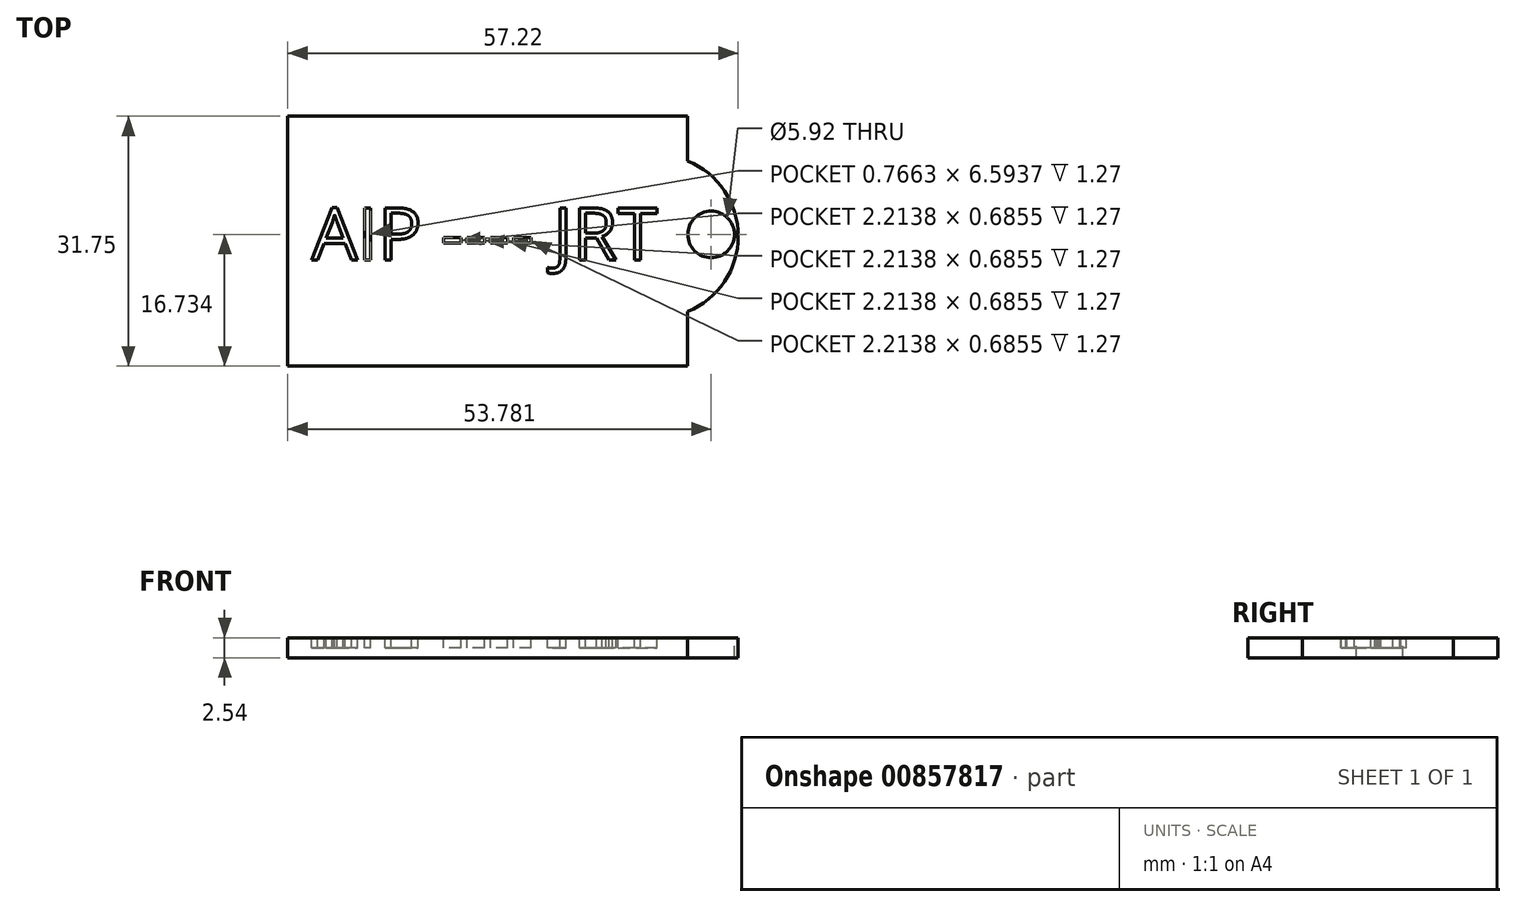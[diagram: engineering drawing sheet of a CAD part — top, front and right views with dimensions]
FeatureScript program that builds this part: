
annotation { "Feature Type Name" : "Feature", "Feature Type Description" : "" }
export const myFeature = defineFeature(function(context is Context, id is Id, definition is map)
    precondition{}
    {
        {
            var Q0;
            Q0=qCreatedBy(makeId("Top.planeOp"),FACE);
            var sketch = newSketch(context, id + "F0", { "sketchPlane" : qUnion([Q0])});
            skLineSegment(sketch, "E0.bottom", {"start": v(0, 0) * mm, "end": v(50.8, 0) * mm});
            skLineSegment(sketch, "E0.top", {"start": v(0, 31.75) * mm, "end": v(50.8, 31.75) * mm});
            skLineSegment(sketch, "E0.left", {"start": v(0, 0) * mm, "end": v(0, 31.75) * mm});
            skLineSegment(sketch, "E0.right", {"start": v(50.8, 0) * mm, "end": v(50.8, 31.75) * mm});
            skSolve(sketch);
        }
        {
            var Q0;
            Q0 = qSketchRegion(id + "F0", true);
            extrude(context, id + "F1", {"entities" : qUnion([Q0]), "depth" : 2.54 * mm, "offsetDistance" : 25.4 * mm});
        }
        {
            var Q0;
            Q0=makeQuery(id+"F1.opExtrude","CAP_FACE",FACE,{"disambiguationData":[OSD([sQuery(id+"F0.wireOp",EDGE,"E0.bottom"),sQuery(id+"F0.wireOp",EDGE,"E0.top"),sQuery(id+"F0.wireOp",EDGE,"E0.left"),sQuery(id+"F0.wireOp",EDGE,"E0.right")])],"isStart":false});
            var sketch = newSketch(context, id + "F2", { "sketchPlane" : qUnion([Q0])});
            skText(sketch, "E1", { "text": "AIP ---- JRT", "fontName": "OpenSans-Regular.ttf"});
            const initialGuessF2  = {"E1": [0.00303, 0.0135, 1, 0, 0.00665]};
            skSetInitialGuess(sketch, initialGuessF2);
            skSolve(sketch);
        }
        {
            var Q0;
            Q0 = qSketchRegion(id + "F2", true);
            extrude(context, id + "F3", {"entities" : qUnion([Q0]), "operationType" : NewBodyOperationType.REMOVE, "oppositeDirection" : true, "depth" : 1.27 * mm, "offsetDistance" : 25.4 * mm});
        }
        {
            var Q0;
            {var subQ0=sQuery(id+"F0.wireOp",EDGE,"E0.left");var subQ1=sQuery(id+"F0.wireOp",EDGE,"E0.bottom");var subQ2=sQuery(id+"F0.wireOp",EDGE,"E0.right");var subQ3=sQuery(id+"F0.wireOp",EDGE,"E0.top");Q0=makeQuery(id+"F3.boolean.opBoolean","SPLIT",FACE,{"disambiguationData":[TD([makeQuery(id+"F1.opExtrude","SWEPT_FACE",FACE,{"disambiguationData":[OSD([subQ1])]})])],"derivedFrom":makeQuery(id+"F1.opExtrude","CAP_FACE",FACE,{"disambiguationData":[OSD([subQ1,subQ3,subQ0,subQ2])],"isStart":false})});}
            var sketch = newSketch(context, id + "F4", { "sketchPlane" : qUnion([Q0])});
            skArc(sketch, "E2", {"start": v(50.8, 6.93) * mm, "mid": v(57.22, 16.5) * mm, "end": v(50.8, 26.07) * mm});
            skSolve(sketch);
        }
        {
            var Q0;
            {var subQ0=sQuery(id+"F4.wireOp",EDGE,"E2");Q0=makeQuery(id+"F4.imprint","IMPRINT",FACE,{"disambiguationData":[TD([[makeQuery(id+"F4.imprint","IMPRINT",EDGE,{"derivedFrom":subQ0}),1.0]])]});}
            var sketch = newSketch(context, id + "F5", { "sketchPlane" : qUnion([Q0])});
            skCircle(sketch, "E3", {"center": v(53.78, 16.73) * mm, "radius": 2.96 * mm});
            skSolve(sketch);
        }
        {
            var Q0;
            {var subQ0=sQuery(id+"F4.wireOp",EDGE,"E2");Q0=makeQuery(id+"F4.imprint","IMPRINT",FACE,{"disambiguationData":[TD([[makeQuery(id+"F4.imprint","IMPRINT",EDGE,{"derivedFrom":subQ0}),1.0]])]});}
            extrude(context, id + "F6", {"entities" : qUnion([Q0]), "operationType" : NewBodyOperationType.ADD, "oppositeDirection" : true, "depth" : 2.54 * mm, "offsetDistance" : 25.4 * mm});
        }
        {
            var Q0;
            Q0=makeQuery(id+"F5.imprint","IMPRINT",FACE,{"disambiguationData":[TD([[makeQuery(id+"F5.imprint","IMPRINT",EDGE,{"derivedFrom":sQuery(id+"F5.wireOp",EDGE,"E3")}),1.0]])]});
            extrude(context, id + "F7", {"entities" : qUnion([Q0]), "operationType" : NewBodyOperationType.REMOVE, "oppositeDirection" : true, "depth" : 25.4 * mm, "offsetDistance" : 25.4 * mm});
        }
    });
